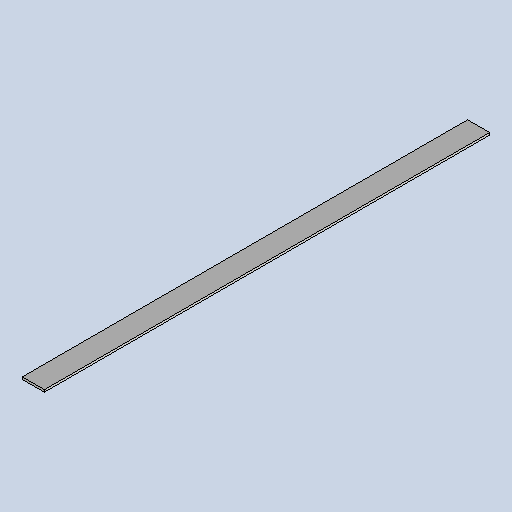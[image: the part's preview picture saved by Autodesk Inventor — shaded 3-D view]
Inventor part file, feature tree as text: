
AUTODESK INVENTOR PART (.ipt)
format: ipt  version: 2025.3 (Build 293356030, 356C)  size: 148,992 bytes
history: native  units: mm
features: other x2, sheet_metal_op x1, sketch x1
ambient origin geometry x8: Origin, YZ Plane, XZ Plane, XY Plane, X Axis, Y Axis, Z Axis, Center Point
bodies: Solid1 (feature_tree)
feature tree (4):
  sheet_metal_op  "Face1"
  sketch  "Sketch1"  dims[d2=20.0mm d3=2.0mm d18=403.0mm]
  other  "Plate1"
  other  "Definition1"
